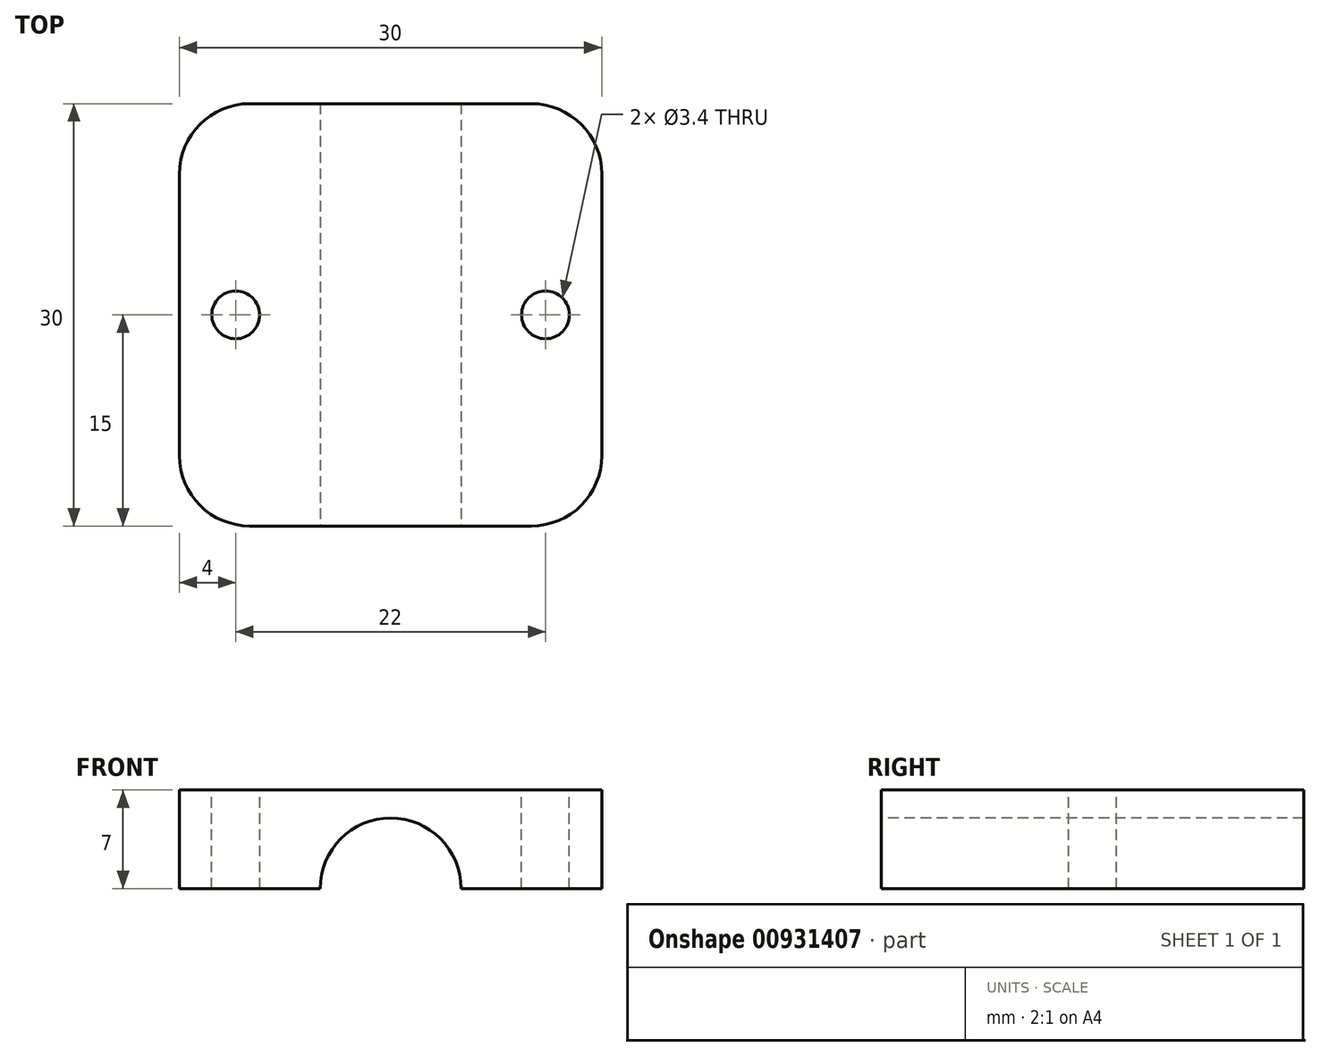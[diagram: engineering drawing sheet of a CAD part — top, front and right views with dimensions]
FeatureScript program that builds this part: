
annotation { "Feature Type Name" : "Feature", "Feature Type Description" : "" }
export const myFeature = defineFeature(function(context is Context, id is Id, definition is map)
    precondition{}
    {
        {
            var Q0;
            Q0=qCreatedBy(makeId("Top.planeOp"),FACE);
            var sketch = newSketch(context, id + "F0", { "sketchPlane" : qUnion([Q0])});
            skLineSegment(sketch, "E0.bottom", {"start": v(15, -15) * mm, "end": v(-15, -15) * mm});
            skLineSegment(sketch, "E0.top", {"start": v(15, 15) * mm, "end": v(-15, 15) * mm});
            skLineSegment(sketch, "E0.left", {"start": v(15, -15) * mm, "end": v(15, 15) * mm});
            skLineSegment(sketch, "E0.right", {"start": v(-15, -15) * mm, "end": v(-15, 15) * mm});
            skPoint(sketch, "E0.middle", {"position": v(0, 0) * mm});
            skSolve(sketch);
        }
        {
            var Q0;
            Q0=makeQuery(id+"F0.imprint","IMPRINT",FACE,{"disambiguationData":[TD([[makeQuery(id+"F0.imprint","IMPRINT",EDGE,{"derivedFrom":sQuery(id+"F0.wireOp",EDGE,"E0.bottom")}),-1.0]])]});
            extrude(context, id + "F1", {"entities" : qUnion([Q0]), "depth" : 7 * mm, "offsetDistance" : 25 * mm});
        }
        {
            var Q0;
            Q0=makeQuery(id+"F1.opExtrude","CAP_FACE",FACE,{"disambiguationData":[OSD([sQuery(id+"F0.wireOp",EDGE,"E0.bottom"),sQuery(id+"F0.wireOp",EDGE,"E0.top"),sQuery(id+"F0.wireOp",EDGE,"E0.left"),sQuery(id+"F0.wireOp",EDGE,"E0.right")])],"isStart":false});
            var sketch = newSketch(context, id + "F2", { "sketchPlane" : qUnion([Q0])});
            skPoint(sketch, "E1", {"position": v(-11, 0) * mm});
            skPoint(sketch, "E2", {"position": v(11, 0) * mm});
            skSolve(sketch);
        }
        {
            var Q0;
            Q0=sQuery(id+"F2.wireOp",VERTEX,"E1");
            var Q1;
            Q1=sQuery(id+"F2.wireOp",VERTEX,"E2");
            var Q2;
            Q2=makeQuery(id+"F1.opExtrude","SWEPT_BODY",BODY,{"disambiguationData":[OSD([sQuery(id+"F0.wireOp",EDGE,"E0.bottom"),sQuery(id+"F0.wireOp",EDGE,"E0.top"),sQuery(id+"F0.wireOp",EDGE,"E0.left"),sQuery(id+"F0.wireOp",EDGE,"E0.right")])]});
            hole(context, id + "F3", {"style" : HoleStyle.SIMPLE, "endStyle" : HoleEndStyle.THROUGH, "standardTappedOrClearance" : lookupTablePath({ "fit" : "Normal", "standard" : "ISO", "size" : "M3", "type" : "Clearance" }), "standardBlindInLast" : lookupTablePath({ "fit" : "Normal", "standard" : "ISO", "engagement" : "75%", "pitch" : "0.5 mm", "size" : "M3", "type" : "Clearance & tapped" }), "holeDiameter" : 3.4 * mm, "majorDiameter" : 5 * mm, "isTappedThrough" : true, "tappedDepth" : 12 * mm, "tapClearance" : 3, "locations" : qUnion([Q0, Q1]), "scope" : qUnion([Q2])});
        }
        {
            var Q0;
            Q0=makeQuery(id+"F1.opExtrude","SWEPT_FACE",FACE,{"disambiguationData":[OSD([sQuery(id+"F0.wireOp",EDGE,"E0.bottom")])]});
            var sketch = newSketch(context, id + "F4", { "sketchPlane" : qUnion([Q0])});
            skCircle(sketch, "E3", {"center": v(0, 0) * mm, "radius": 5 * mm});
            skSolve(sketch);
        }
        {
            var Q0;
            {var subQ0=sQuery(id+"F4.wireOp",EDGE,"E3");var subQ1=makeQuery(id+"F1.opExtrude","CAP_EDGE",EDGE,{"disambiguationData":[OSD([sQuery(id+"F0.wireOp",EDGE,"E0.bottom")])],"isStart":true});var subQ2=makeQuery(id+"F4.imprint","INTERSECT",VERTEX,{"disambiguationData":[OD(0.0)],"derivedFrom":[subQ1,subQ0]});Q0=makeQuery(id+"F4.imprint","IMPRINT",FACE,{"disambiguationData":[TD([[makeQuery(id+"F4.imprint","IMPRINT",EDGE,{"disambiguationData":[TD([[subQ2,-1.0]])],"derivedFrom":subQ0}),1.0]])]});}
            extrude(context, id + "F5", {"entities" : qUnion([Q0]), "operationType" : NewBodyOperationType.REMOVE, "endBound" : BoundingType.UP_TO_NEXT, "oppositeDirection" : true, "depth" : 25 * mm, "offsetDistance" : 25 * mm});
        }
        {
            var Q0;
            Q0=makeQuery(id+"F1.opExtrude","SWEPT_EDGE",EDGE,{"disambiguationData":[OSD([sQuery(id+"F0.wireOp",EDGE,"E0.bottom"),sQuery(id+"F0.wireOp",EDGE,"E0.left")])]});
            var Q1;
            Q1=makeQuery(id+"F1.opExtrude","SWEPT_EDGE",EDGE,{"disambiguationData":[OSD([sQuery(id+"F0.wireOp",EDGE,"E0.bottom"),sQuery(id+"F0.wireOp",EDGE,"E0.right")])]});
            var Q2;
            Q2=makeQuery(id+"F1.opExtrude","SWEPT_EDGE",EDGE,{"disambiguationData":[OSD([sQuery(id+"F0.wireOp",EDGE,"E0.top"),sQuery(id+"F0.wireOp",EDGE,"E0.left")])]});
            var Q3;
            Q3=makeQuery(id+"F1.opExtrude","SWEPT_EDGE",EDGE,{"disambiguationData":[OSD([sQuery(id+"F0.wireOp",EDGE,"E0.top"),sQuery(id+"F0.wireOp",EDGE,"E0.right")])]});
            fillet(context, id + "F6", {"entities" : qUnion([Q0, Q1, Q2, Q3]), "radius" : 5 * mm, "tangentPropagation" : true, "allowEdgeOverflow" : false});
        }
    });
